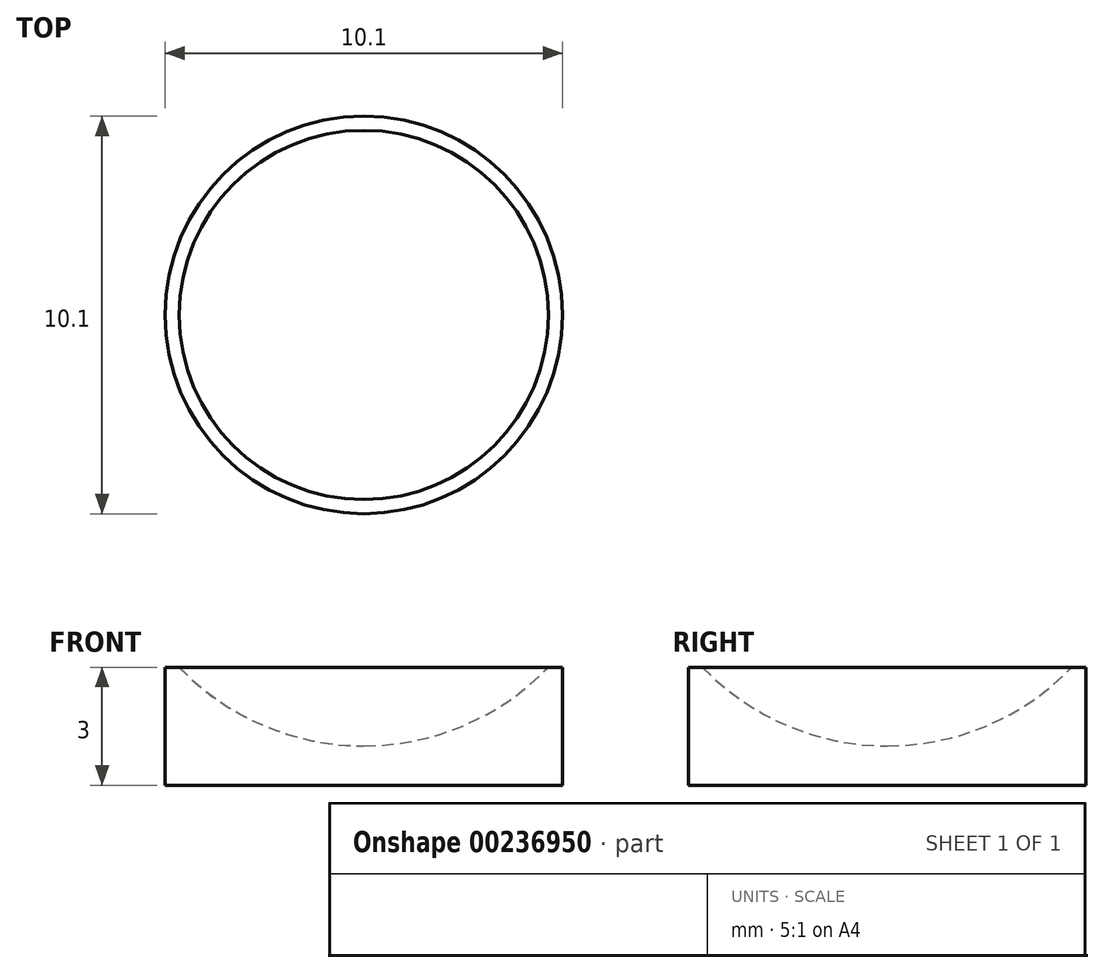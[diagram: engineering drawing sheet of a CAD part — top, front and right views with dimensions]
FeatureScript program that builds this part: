
annotation { "Feature Type Name" : "Feature", "Feature Type Description" : "" }
export const myFeature = defineFeature(function(context is Context, id is Id, definition is map)
    precondition{}
    {
        {
            var Q0;
            Q0=qCreatedBy(makeId("Top.planeOp"),FACE);
            var sketch = newSketch(context, id + "F0", { "sketchPlane" : qUnion([Q0])});
            skCircle(sketch, "E0", {"center": v(0, 0) * mm, "radius": 5.05 * mm});
            skSolve(sketch);
        }
        {
            var Q0;
            Q0 = qSketchRegion(id + "F0", true);
            extrude(context, id + "F1", {"entities" : qUnion([Q0]), "depth" : 3 * mm});
        }
        {
            var Q0;
            Q0=qCreatedBy(makeId("Front.planeOp"),FACE);
            var sketch = newSketch(context, id + "F2", { "sketchPlane" : qUnion([Q0])});
            skCircle(sketch, "E1", {"center": v(0, 7.5) * mm, "radius": 6.5 * mm});
            skLineSegment(sketch, "E2", {"start": v(0, 14) * mm, "end": v(0, 1) * mm});
            skSolve(sketch);
        }
        {
            var Q0;
            {var subQ0=sQuery(id+"F2.wireOp",EDGE,"E2");Q0=makeQuery(id+"F2.imprint","IMPRINT",FACE,{"disambiguationData":[TD([[makeQuery(id+"F2.imprint","IMPRINT",EDGE,{"derivedFrom":subQ0}),1.0]])]});}
            var Q1;
            Q1=sQuery(id+"F2.wireOp",EDGE,"E2");
            revolve(context, id + "F3", {"operationType" : NewBodyOperationType.REMOVE, "entities" : qUnion([Q0]), "axis" : qUnion([Q1]), "revolveType" : RevolveType.FULL, "oppositeDirection" : true});
        }
    });
